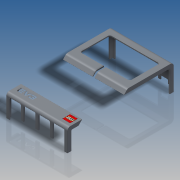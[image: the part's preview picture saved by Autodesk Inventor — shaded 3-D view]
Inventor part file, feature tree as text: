
AUTODESK INVENTOR PART (.ipt)
format: ipt  version: 2016 SP2 (Build 200236200, 236)  size: 760,832 bytes
history: native  units: in
note: dims shown in document units (in); Inventor stores cm internally (conversion verified against a paired STEP export)
features: extrude x7, sketch x6, other x2, fillet x2, projected_geometry x1
ambient origin geometry x8: Origin, YZ Plane, XZ Plane, XY Plane, X Axis, Y Axis, Z Axis, Center Point
bodies: Solid1 (feature_tree)
feature tree (18):
  sketch  "Sketch2"  dims[d0=0.1575in d1=2.0472in]
  extrude  "Extrusion1"  Depth=2.0472in
  extrude  "Extrusion2"  Depth=0.1417in
  extrude  "Extrusion3"  Depth=0.1575in
  extrude  "Extrusion4"  Depth=0.0351in
  extrude  "Extrusion5"  Depth=1.7165in
  sketch  "Sketch6"  dims[d10=0.1417in d11=1.7165in]
  extrude  "Extrusion6"  Depth=0.0039in
  extrude  "Extrusion7"  Depth=0.0039in
  other  "Decal2"
  fillet  "Fillet2"  Radius=0.0472in
  fillet  "Fillet3"  Radius=0.0472in
  sketch  "Sketch3"  dims[d2=1.0709in d3=0.1417in]
  sketch  "Sketch4"  dims[d4=0.0472in d5=0.1575in]
  sketch  "Sketch5"  dims[d8=0.3298in d9=0.0351in]
  projected_geometry  "Projected Loop1"
  other  "Image1"
  sketch  "Sketch7"  dims[d12=0.1197in d13=0.1575in d14=0.1575in d15=0.0472in d16=0.0472in d17=0.9134in d18=0.6142in d19=0.0472in d20=0.063in d21=0.063in d22=2.5197in d23=0.0in d24=2.4252in d25=0.0in d26=0.0787in d27=2.0472in d28=0.0787in d29=1.2283in d30=0.3465in d31=2.4252in d32=0.0in d33=0.126in d34=0.2205in d35=0.315in d36=0.1575in d37=0.189in d38=0.0315in d39=0.5984in d40=0.126in d41=0.7937in d42=0.0378in d43=2.4252in d44=0.0in d45=0.126in d46=0.4724in d47=0.0378in d48=0.2205in d49=0.7937in d50=2.4252in d51=0.0in d53=0.315in d59=0.0787in d60=0.1102in d177=0.2016in d178=0.2016in d179=0.0551in d180=0.0146in d181=0.0069in d182=0.0614in d183=0.2381in d184=0.085in d185=0.0626in d186=0.0117in d187=0.0104in d188=0.0057in d197=0.0029in d198=0.0015in d199=0.0013in d200=0.0057in d205=0.062in d206=45.0deg d208=45.0deg d209=0.0535in d210=0.8392in d211=0.0455in d212=0.0186in d220=0.1354in d221=0.1512in d226=0.0099in d228=0.0557in d229=0.0724in d230=0.0604in d231=0.062in d232=0.2016in d233=0.0545in d234=0.0074in d235=0.0598in d236=0.0316in d237=0.0099in d238=45.0deg d239=0.0146in d240=0.0623in d241=0.0099in d242=0.3078in d243=0.9268in d244=0.009in d247=0.0083in d252=0.0316in d253=0.0in d254=0.0in d255=0.0in d256=0.0in d257=0.0in d258=0.0in d259=0.0in d260=0.0in d261=0.0in d262=0.0in d263=0.0in d264=0.0in d265=0.0in d266=0.0in d267=0.0in d268=0.0in d269=0.0in d270=0.0in d271=0.0in d272=0.0in d274=0.3465in d276=0.685in d277=0.0409in d278=0.0in d279=0.0079in d280=-0.3092in d281=0.7717in d283=0.0472in d284=0.0472in d285=0.0472in d287=0.0039in d288=0.0039in]
